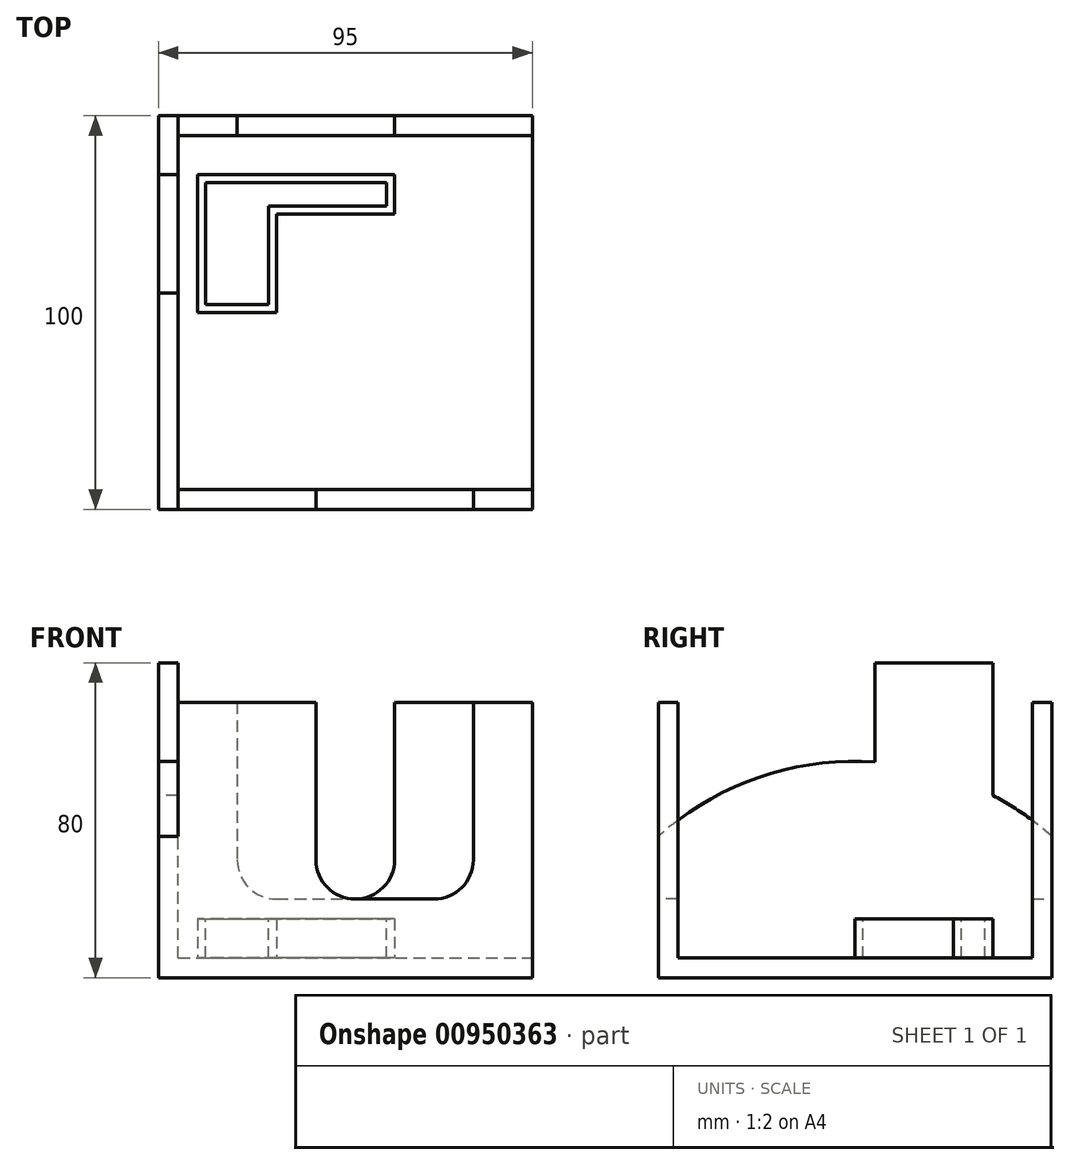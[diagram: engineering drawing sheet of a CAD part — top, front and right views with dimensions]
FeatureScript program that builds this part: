
annotation { "Feature Type Name" : "Feature", "Feature Type Description" : "" }
export const myFeature = defineFeature(function(context is Context, id is Id, definition is map)
    precondition{}
    {
        {
            var Q0;
            Q0=qCreatedBy(makeId("Top.planeOp"),FACE);
            var sketch = newSketch(context, id + "F0", { "sketchPlane" : qUnion([Q0])});
            skLineSegment(sketch, "E0.bottom", {"start": v(0, 0) * mm, "end": v(95, 0) * mm});
            skLineSegment(sketch, "E0.top", {"start": v(0, 100) * mm, "end": v(95, 100) * mm});
            skLineSegment(sketch, "E0.left", {"start": v(0, 0) * mm, "end": v(0, 100) * mm});
            skLineSegment(sketch, "E0.right", {"start": v(95, 0) * mm, "end": v(95, 100) * mm});
            skSolve(sketch);
        }
        {
            var Q0;
            Q0 = qSketchRegion(id + "F0", true);
            extrude(context, id + "F1", {"entities" : qUnion([Q0]), "depth" : 5 * mm, "offsetDistance" : 25 * mm});
        }
        {
            var Q0;
            Q0=makeQuery(id+"F1.opExtrude","SWEPT_FACE",FACE,{"disambiguationData":[OSD([sQuery(id+"F0.wireOp",EDGE,"E0.left")])]});
            var sketch = newSketch(context, id + "F2", { "sketchPlane" : qUnion([Q0])});
            skArc(sketch, "E1", {"start": v(0, 35.9) * mm, "mid": v(-25.59, 50.92) * mm, "end": v(-55, 54.83) * mm});
            skLineSegment(sketch, "E2", {"start": v(-55, 54.83) * mm, "end": v(-55, 80) * mm});
            skLineSegment(sketch, "E3", {"start": v(-55, 80) * mm, "end": v(-85, 80) * mm});
            skLineSegment(sketch, "E4", {"start": v(-85, 80) * mm, "end": v(-85, 46.33) * mm});
            skLineSegment(sketch, "E5", {"start": v(0, 5) * mm, "end": v(0, 35.9) * mm});
            skLineSegment(sketch, "E6", {"start": v(0, 5) * mm, "end": v(-100, 5) * mm});
            skLineSegment(sketch, "E7", {"start": v(-100, 5) * mm, "end": v(-100, 35.9) * mm});
            skArc(sketch, "E8.trimOffspring", {"start": v(-85, 46.33) * mm, "mid": v(-92.82, 41.58) * mm, "end": v(-100, 35.9) * mm});
            skSolve(sketch);
        }
        {
            var Q0;
            Q0 = qSketchRegion(id + "F2", true);
            extrude(context, id + "F3", {"entities" : qUnion([Q0]), "operationType" : NewBodyOperationType.ADD, "oppositeDirection" : true, "depth" : 5 * mm, "offsetDistance" : 25 * mm});
        }
        {
            var Q0;
            Q0=makeQuery(id+"F3.boolean.opBoolean","MERGE",FACE,{"derivedFrom":[makeQuery(id+"F1.opExtrude","SWEPT_FACE",FACE,{"disambiguationData":[OSD([sQuery(id+"F0.wireOp",EDGE,"E0.bottom")])]}),makeQuery(id+"F3.opExtrude","SWEPT_FACE",FACE,{"disambiguationData":[OSD([sQuery(id+"F2.wireOp",EDGE,"E5")])]})]});
            var sketch = newSketch(context, id + "F4", { "sketchPlane" : qUnion([Q0])});
            skLineSegment(sketch, "E9", {"start": v(5, 5) * mm, "end": v(5, 70) * mm});
            skLineSegment(sketch, "E10", {"start": v(5, 70) * mm, "end": v(40, 70) * mm});
            skLineSegment(sketch, "E11", {"start": v(40, 70) * mm, "end": v(40, 20) * mm});
            skLineSegment(sketch, "E12", {"start": v(40, 20) * mm, "end": v(80, 20) * mm});
            skLineSegment(sketch, "E13", {"start": v(80, 20) * mm, "end": v(80, 70) * mm});
            skLineSegment(sketch, "E14", {"start": v(80, 70) * mm, "end": v(95, 70) * mm});
            skLineSegment(sketch, "E15", {"start": v(95, 70) * mm, "end": v(95, 5) * mm});
            skLineSegment(sketch, "E16", {"start": v(95, 5) * mm, "end": v(5, 5) * mm});
            skSolve(sketch);
        }
        {
            var Q0;
            Q0 = qSketchRegion(id + "F4", true);
            extrude(context, id + "F5", {"entities" : qUnion([Q0]), "operationType" : NewBodyOperationType.ADD, "oppositeDirection" : true, "depth" : 5 * mm, "offsetDistance" : 25 * mm});
        }
        {
            var Q0;
            Q0=makeQuery(id+"F3.boolean.opBoolean","MERGE",FACE,{"derivedFrom":[makeQuery(id+"F1.opExtrude","SWEPT_FACE",FACE,{"disambiguationData":[OSD([sQuery(id+"F0.wireOp",EDGE,"E0.top")])]}),makeQuery(id+"F3.opExtrude","SWEPT_FACE",FACE,{"disambiguationData":[OSD([sQuery(id+"F2.wireOp",EDGE,"E7")])]})]});
            var sketch = newSketch(context, id + "F6", { "sketchPlane" : qUnion([Q0])});
            skLineSegment(sketch, "E17", {"start": v(-5, 5) * mm, "end": v(-5, 70) * mm});
            skLineSegment(sketch, "E18", {"start": v(-5, 70) * mm, "end": v(-20, 70) * mm});
            skLineSegment(sketch, "E19", {"start": v(-20, 70) * mm, "end": v(-20, 20) * mm});
            skLineSegment(sketch, "E20", {"start": v(-20, 20) * mm, "end": v(-60, 20) * mm});
            skLineSegment(sketch, "E21", {"start": v(-60, 20) * mm, "end": v(-60, 70) * mm});
            skLineSegment(sketch, "E22", {"start": v(-60, 70) * mm, "end": v(-95, 70) * mm});
            skLineSegment(sketch, "E23", {"start": v(-95, 70) * mm, "end": v(-95, 5) * mm});
            skLineSegment(sketch, "E24", {"start": v(-95, 5) * mm, "end": v(-5, 5) * mm});
            skSolve(sketch);
        }
        {
            var Q0;
            Q0 = qSketchRegion(id + "F6", true);
            extrude(context, id + "F7", {"entities" : qUnion([Q0]), "operationType" : NewBodyOperationType.ADD, "oppositeDirection" : true, "depth" : 5 * mm, "offsetDistance" : 25 * mm});
        }
        {
            var Q0;
            Q0=makeQuery(id+"F7.opExtrude","SWEPT_EDGE",EDGE,{"disambiguationData":[OSD([sQuery(id+"F6.wireOp",EDGE,"E19"),sQuery(id+"F6.wireOp",EDGE,"E20")])]});
            var Q1;
            Q1=makeQuery(id+"F5.opExtrude","SWEPT_EDGE",EDGE,{"disambiguationData":[OSD([sQuery(id+"F4.wireOp",EDGE,"E11"),sQuery(id+"F4.wireOp",EDGE,"E12")])]});
            var Q2;
            Q2=makeQuery(id+"F7.opExtrude","SWEPT_EDGE",EDGE,{"disambiguationData":[OSD([sQuery(id+"F6.wireOp",EDGE,"E20"),sQuery(id+"F6.wireOp",EDGE,"E21")])]});
            var Q3;
            Q3=makeQuery(id+"F5.opExtrude","SWEPT_EDGE",EDGE,{"disambiguationData":[OSD([sQuery(id+"F4.wireOp",EDGE,"E12"),sQuery(id+"F4.wireOp",EDGE,"E13")])]});
            fillet(context, id + "F8", {"entities" : qUnion([Q0, Q1, Q2, Q3]), "radius" : 10 * mm, "tangentPropagation" : true, "allowEdgeOverflow" : false});
        }
        {
            var Q0;
            Q0=makeQuery(id+"F1.opExtrude","CAP_FACE",FACE,{"disambiguationData":[OSD([sQuery(id+"F0.wireOp",EDGE,"E0.bottom"),sQuery(id+"F0.wireOp",EDGE,"E0.top"),sQuery(id+"F0.wireOp",EDGE,"E0.left"),sQuery(id+"F0.wireOp",EDGE,"E0.right")])],"isStart":false});
            var sketch = newSketch(context, id + "F9", { "sketchPlane" : qUnion([Q0])});
            skLineSegment(sketch, "E25", {"start": v(10, 50) * mm, "end": v(10, 85) * mm});
            skLineSegment(sketch, "E26", {"start": v(10, 85) * mm, "end": v(60, 85) * mm});
            skLineSegment(sketch, "E27", {"start": v(60, 85) * mm, "end": v(60, 75) * mm});
            skLineSegment(sketch, "E28", {"start": v(60, 75) * mm, "end": v(30, 75) * mm});
            skLineSegment(sketch, "E29", {"start": v(30, 75) * mm, "end": v(30, 50) * mm});
            skLineSegment(sketch, "E30", {"start": v(30, 50) * mm, "end": v(10, 50) * mm});
            skSolve(sketch);
        }
        {
            var Q0;
            Q0 = qSketchRegion(id + "F9", true);
            extrude(context, id + "F10", {"entities" : qUnion([Q0]), "operationType" : NewBodyOperationType.ADD, "depth" : 10 * mm, "offsetDistance" : 25 * mm});
        }
        {
            var Q0;
            Q0=makeQuery(id+"F10.opExtrude","CAP_FACE",FACE,{"disambiguationData":[OSD([sQuery(id+"F9.wireOp",EDGE,"E25"),sQuery(id+"F9.wireOp",EDGE,"E26"),sQuery(id+"F9.wireOp",EDGE,"E27"),sQuery(id+"F9.wireOp",EDGE,"E28"),sQuery(id+"F9.wireOp",EDGE,"E29"),sQuery(id+"F9.wireOp",EDGE,"E30")])],"isStart":false});
            var sketch = newSketch(context, id + "F11", { "sketchPlane" : qUnion([Q0])});
            skLineSegment(sketch, "E31.0", {"start": v(12, 83) * mm, "end": v(12, 52) * mm});
            skLineSegment(sketch, "E31.1", {"start": v(28, 52) * mm, "end": v(28, 77) * mm});
            skLineSegment(sketch, "E31.2", {"start": v(28, 77) * mm, "end": v(58, 77) * mm});
            skLineSegment(sketch, "E31.3", {"start": v(12, 52) * mm, "end": v(28, 52) * mm});
            skLineSegment(sketch, "E31.4", {"start": v(58, 77) * mm, "end": v(58, 83) * mm});
            skLineSegment(sketch, "E31.5", {"start": v(58, 83) * mm, "end": v(12, 83) * mm});
            skSolve(sketch);
        }
        {
            var Q0;
            Q0=makeQuery(id+"F11.imprint","IMPRINT",FACE,{"disambiguationData":[TD([[makeQuery(id+"F11.imprint","IMPRINT",EDGE,{"derivedFrom":sQuery(id+"F11.wireOp",EDGE,"E31.0")}),1.0]])]});
            extrude(context, id + "F12", {"entities" : qUnion([Q0]), "operationType" : NewBodyOperationType.REMOVE, "oppositeDirection" : true, "depth" : 10 * mm, "offsetDistance" : 25 * mm});
        }
    });
